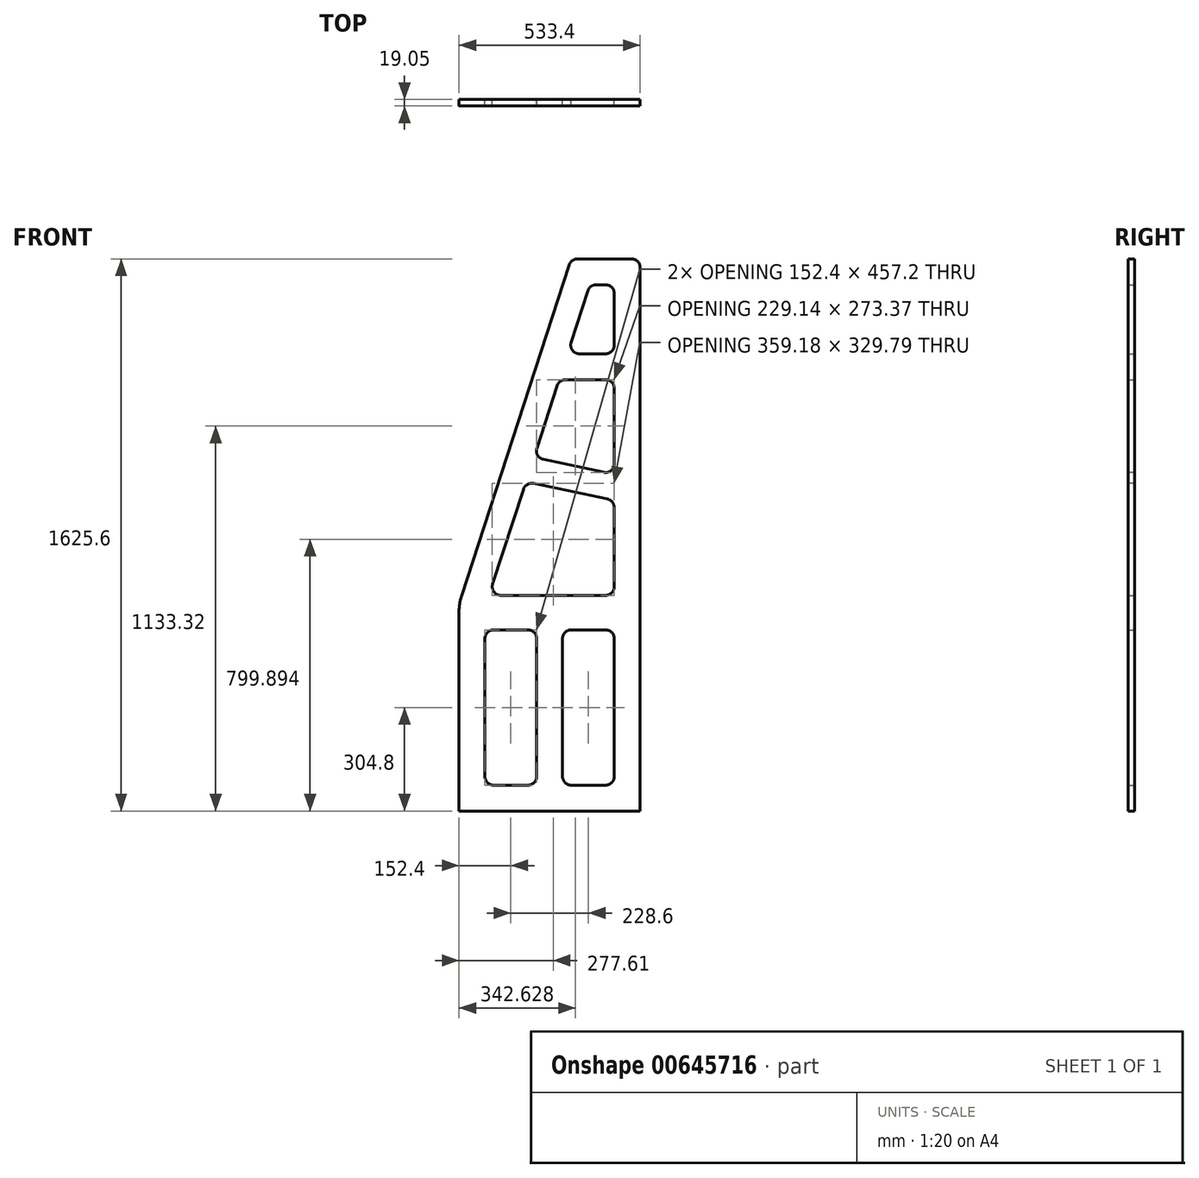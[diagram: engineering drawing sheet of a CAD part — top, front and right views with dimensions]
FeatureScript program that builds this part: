
annotation { "Feature Type Name" : "Feature", "Feature Type Description" : "" }
export const myFeature = defineFeature(function(context is Context, id is Id, definition is map)
    precondition{}
    {
        {
            var Q0;
            Q0=qCreatedBy(makeId("Front.planeOp"),FACE);
            var sketch = newSketch(context, id + "F0", { "sketchPlane" : qUnion([Q0])});
            skLineSegment(sketch, "E0.bottom", {"start": v(266.7, 812.8) * mm, "end": v(63.5, 812.8) * mm});
            skLineSegment(sketch, "E0.top", {"start": v(266.7, -812.8) * mm, "end": v(-266.7, -812.8) * mm});
            skLineSegment(sketch, "E0.left", {"start": v(266.7, 812.8) * mm, "end": v(266.7, -812.8) * mm});
            skLineSegment(sketch, "E0.right", {"start": v(-266.7, -203.2) * mm, "end": v(-266.7, -812.8) * mm});
            skPoint(sketch, "E0.middle", {"position": v(0, 0) * mm});
            skLineSegment(sketch, "E1", {"start": v(-266.7, -203.2) * mm, "end": v(63.5, 812.8) * mm});
            skPoint(sketch, "E2.orphan", {"position": v(-266.7, 812.8) * mm});
            skPoint(sketch, "E3", {"position": v(-190.5, -736.6) * mm});
            skPoint(sketch, "E4", {"position": v(190.5, -736.6) * mm});
            skPoint(sketch, "E5", {"position": v(190.5, -279.4) * mm});
            skPoint(sketch, "E6", {"position": v(38.1, -279.4) * mm});
            skPoint(sketch, "E7", {"position": v(38.1, -736.6) * mm});
            skPoint(sketch, "E8", {"position": v(-38.1, -279.4) * mm});
            skPoint(sketch, "E9", {"position": v(-38.1, -736.6) * mm});
            skPoint(sketch, "E10", {"position": v(-190.5, -279.4) * mm});
            skPoint(sketch, "E11", {"position": v(-178.32, -177.8) * mm});
            skPoint(sketch, "E12", {"position": v(190.5, -177.8) * mm});
            skPoint(sketch, "E13", {"position": v(190.5, 127) * mm});
            skPoint(sketch, "E14", {"position": v(-79.26, 127) * mm});
            skPoint(sketch, "E15", {"position": v(190.5, 228.6) * mm});
            skPoint(sketch, "E16", {"position": v(190.5, 736.6) * mm});
            skPoint(sketch, "E17", {"position": v(190.5, 457.2) * mm});
            skLineSegment(sketch, "E18", {"start": v(-190.5, -279.4) * mm, "end": v(-38.1, -279.4) * mm});
            skLineSegment(sketch, "E19", {"start": v(-38.1, -736.6) * mm, "end": v(-190.5, -736.6) * mm});
            skLineSegment(sketch, "E20", {"start": v(-190.5, -279.4) * mm, "end": v(-190.5, -736.6) * mm});
            skLineSegment(sketch, "E21", {"start": v(-38.1, -736.6) * mm, "end": v(-38.1, -279.4) * mm});
            skLineSegment(sketch, "E22", {"start": v(38.1, -279.4) * mm, "end": v(38.1, -736.6) * mm});
            skLineSegment(sketch, "E23", {"start": v(38.1, -736.6) * mm, "end": v(190.5, -736.6) * mm});
            skLineSegment(sketch, "E24", {"start": v(190.5, -736.6) * mm, "end": v(190.5, -279.4) * mm});
            skLineSegment(sketch, "E25", {"start": v(38.1, -279.4) * mm, "end": v(190.5, -279.4) * mm});
            skLineSegment(sketch, "E26", {"start": v(-178.32, -177.8) * mm, "end": v(-79.26, 127) * mm});
            skLineSegment(sketch, "E27", {"start": v(-178.32, -177.8) * mm, "end": v(190.5, -177.8) * mm});
            skLineSegment(sketch, "E28", {"start": v(190.5, -177.8) * mm, "end": v(190.5, 127) * mm});
            skPoint(sketch, "E29", {"position": v(-46.24, 228.6) * mm});
            skLineSegment(sketch, "E30", {"start": v(190.5, 228.6) * mm, "end": v(190.5, 457.2) * mm});
            skPoint(sketch, "E31", {"position": v(28.05, 457.2) * mm});
            skPoint(sketch, "E32", {"position": v(190.5, 533.4) * mm});
            skPoint(sketch, "E33", {"position": v(52.82, 533.4) * mm});
            skLineSegment(sketch, "E34", {"start": v(28.05, 457.2) * mm, "end": v(190.5, 457.2) * mm});
            skLineSegment(sketch, "E35", {"start": v(28.05, 457.2) * mm, "end": v(-46.24, 228.6) * mm});
            skLineSegment(sketch, "E36", {"start": v(190.5, 736.6) * mm, "end": v(190.5, 533.4) * mm});
            skLineSegment(sketch, "E37", {"start": v(190.5, 533.4) * mm, "end": v(52.82, 533.4) * mm});
            skLineSegment(sketch, "E38", {"start": v(190.5, 736.6) * mm, "end": v(118.68, 736.6) * mm});
            skLineSegment(sketch, "E39", {"start": v(52.82, 533.4) * mm, "end": v(118.68, 736.6) * mm});
            skPoint(sketch, "E40", {"position": v(190.5, 101.6) * mm});
            skPoint(sketch, "E41", {"position": v(190.5, 177.8) * mm});
            skLineSegment(sketch, "E42", {"start": v(-46.24, 228.6) * mm, "end": v(190.5, 177.8) * mm});
            skLineSegment(sketch, "E43", {"start": v(190.5, 177.8) * mm, "end": v(190.5, 228.6) * mm});
            skPoint(sketch, "E44", {"position": v(-69.8, 156.13) * mm});
            skLineSegment(sketch, "E45", {"start": v(-69.8, 156.13) * mm, "end": v(190.5, 101.6) * mm});
            skLineSegment(sketch, "E46", {"start": v(-79.26, 127) * mm, "end": v(-69.8, 156.13) * mm});
            skSolve(sketch);
        }
        {
            var Q0;
            Q0=makeQuery(id+"F0.imprint","IMPRINT",FACE,{"disambiguationData":[TD([[makeQuery(id+"F0.imprint","IMPRINT",EDGE,{"derivedFrom":sQuery(id+"F0.wireOp",EDGE,"E0.bottom")}),1.0]])]});
            extrude(context, id + "F1", {"entities" : qUnion([Q0]), "depth" : 19.05 * mm, "offsetDistance" : 25.4 * mm});
        }
        {
            var Q0;
            Q0=makeQuery(id+"F1.opExtrude","SWEPT_EDGE",EDGE,{"disambiguationData":[OSD([sQuery(id+"F0.wireOp",EDGE,"E34"),sQuery(id+"F0.wireOp",EDGE,"E35")])]});
            var Q1;
            Q1=makeQuery(id+"F1.opExtrude","SWEPT_EDGE",EDGE,{"disambiguationData":[OSD([sQuery(id+"F0.wireOp",EDGE,"E26"),sQuery(id+"F0.wireOp",EDGE,"GGdQVLDd-dLc8-iVr0-vvL2-QloLVLs5YIJa")])]});
            var Q2;
            Q2=makeQuery(id+"F1.opExtrude","SWEPT_EDGE",EDGE,{"disambiguationData":[OSD([sQuery(id+"F0.wireOp",EDGE,"E18"),sQuery(id+"F0.wireOp",EDGE,"E20")])]});
            var Q3;
            Q3=makeQuery(id+"F1.opExtrude","SWEPT_EDGE",EDGE,{"disambiguationData":[OSD([sQuery(id+"F0.wireOp",EDGE,"E22"),sQuery(id+"F0.wireOp",EDGE,"E25")])]});
            var Q4;
            Q4=makeQuery(id+"F1.opExtrude","SWEPT_EDGE",EDGE,{"disambiguationData":[OSD([sQuery(id+"F0.wireOp",EDGE,"E18"),sQuery(id+"F0.wireOp",EDGE,"E21")])]});
            var Q5;
            Q5=makeQuery(id+"F1.opExtrude","SWEPT_EDGE",EDGE,{"disambiguationData":[OSD([sQuery(id+"F0.wireOp",EDGE,"E24"),sQuery(id+"F0.wireOp",EDGE,"E25")])]});
            var Q6;
            Q6=makeQuery(id+"F1.opExtrude","SWEPT_EDGE",EDGE,{"disambiguationData":[OSD([sQuery(id+"F0.wireOp",EDGE,"GGdQVLDd-dLc8-iVr0-vvL2-QloLVLs5YIJa"),sQuery(id+"F0.wireOp",EDGE,"E28")])]});
            var Q7;
            Q7=makeQuery(id+"F1.opExtrude","SWEPT_EDGE",EDGE,{"disambiguationData":[OSD([sQuery(id+"F0.wireOp",EDGE,"E30"),sQuery(id+"F0.wireOp",EDGE,"E34")])]});
            var Q8;
            Q8=makeQuery(id+"F1.opExtrude","SWEPT_EDGE",EDGE,{"disambiguationData":[OSD([sQuery(id+"F0.wireOp",EDGE,"E27"),sQuery(id+"F0.wireOp",EDGE,"E28")])]});
            var Q9;
            Q9=makeQuery(id+"F1.opExtrude","SWEPT_EDGE",EDGE,{"disambiguationData":[OSD([sQuery(id+"F0.wireOp",EDGE,"E19"),sQuery(id+"F0.wireOp",EDGE,"E20")])]});
            var Q10;
            Q10=makeQuery(id+"F1.opExtrude","SWEPT_EDGE",EDGE,{"disambiguationData":[OSD([sQuery(id+"F0.wireOp",EDGE,"E22"),sQuery(id+"F0.wireOp",EDGE,"E23")])]});
            var Q11;
            Q11=makeQuery(id+"F1.opExtrude","SWEPT_EDGE",EDGE,{"disambiguationData":[OSD([sQuery(id+"F0.wireOp",EDGE,"E19"),sQuery(id+"F0.wireOp",EDGE,"E21")])]});
            var Q12;
            Q12=makeQuery(id+"F1.opExtrude","SWEPT_EDGE",EDGE,{"disambiguationData":[OSD([sQuery(id+"F0.wireOp",EDGE,"E23"),sQuery(id+"F0.wireOp",EDGE,"E24")])]});
            var Q13;
            Q13=makeQuery(id+"F1.opExtrude","SWEPT_EDGE",EDGE,{"disambiguationData":[OSD([sQuery(id+"F0.wireOp",EDGE,"E26"),sQuery(id+"F0.wireOp",EDGE,"E27")])]});
            var Q14;
            Q14=makeQuery(id+"F1.opExtrude","SWEPT_EDGE",EDGE,{"disambiguationData":[OSD([sQuery(id+"F0.wireOp",EDGE,"E67oj2bO-mtO5-RMIz-Xmbo-B9xomXMAUayS"),sQuery(id+"F0.wireOp",EDGE,"E30")])]});
            var Q15;
            Q15=makeQuery(id+"F1.opExtrude","SWEPT_EDGE",EDGE,{"disambiguationData":[OSD([sQuery(id+"F0.wireOp",EDGE,"E67oj2bO-mtO5-RMIz-Xmbo-B9xomXMAUayS"),sQuery(id+"F0.wireOp",EDGE,"E35")])]});
            var Q16;
            Q16=makeQuery(id+"F1.opExtrude","SWEPT_EDGE",EDGE,{"disambiguationData":[OSD([sQuery(id+"F0.wireOp",EDGE,"GkY00ho5-FiLZ-XiAP-ntMC-amQ00H48IU7V"),sQuery(id+"F0.wireOp",EDGE,"E36")])]});
            var Q17;
            Q17=makeQuery(id+"F1.opExtrude","SWEPT_EDGE",EDGE,{"disambiguationData":[OSD([sQuery(id+"F0.wireOp",EDGE,"E36"),sQuery(id+"F0.wireOp",EDGE,"E37")])]});
            var Q18;
            Q18=makeQuery(id+"F1.opExtrude","SWEPT_EDGE",EDGE,{"disambiguationData":[OSD([sQuery(id+"F0.wireOp",EDGE,"eTPufCVI-TwlT-T8aF-QYcv-0YaQZG3wYMVu"),sQuery(id+"F0.wireOp",EDGE,"E37")])]});
            fillet(context, id + "F2", {"entities" : qUnion([Q0, Q1, Q2, Q3, Q4, Q5, Q6, Q7, Q8, Q9, Q10, Q11, Q12, Q13, Q14, Q15, Q16, Q17, Q18]), "radius" : 25.4 * mm, "tangentPropagation" : true, "allowEdgeOverflow" : false});
        }
        {
            var Q0;
            Q0=makeQuery(id+"F1.opExtrude","SWEPT_EDGE",EDGE,{"disambiguationData":[OSD([sQuery(id+"F0.wireOp",EDGE,"E38"),sQuery(id+"F0.wireOp",EDGE,"E39")])]});
            fillet(context, id + "F3", {"entities" : qUnion([Q0]), "radius" : 25.4 * mm, "tangentPropagation" : true, "allowEdgeOverflow" : false});
        }
        {
            var Q0;
            Q0=makeQuery(id+"F1.opExtrude","SWEPT_EDGE",EDGE,{"disambiguationData":[OSD([sQuery(id+"F0.wireOp",EDGE,"E0.right"),sQuery(id+"F0.wireOp",EDGE,"E1")])]});
            fillet(context, id + "F4", {"entities" : qUnion([Q0]), "radius" : 152.4 * mm, "tangentPropagation" : true, "allowEdgeOverflow" : false});
        }
        {
            var Q0;
            Q0=makeQuery(id+"F1.opExtrude","SWEPT_EDGE",EDGE,{"disambiguationData":[OSD([sQuery(id+"F0.wireOp",EDGE,"E0.bottom"),sQuery(id+"F0.wireOp",EDGE,"E0.left")])]});
            var Q1;
            Q1=makeQuery(id+"F1.opExtrude","SWEPT_EDGE",EDGE,{"disambiguationData":[OSD([sQuery(id+"F0.wireOp",EDGE,"E0.bottom"),sQuery(id+"F0.wireOp",EDGE,"E1")])]});
            fillet(context, id + "F5", {"entities" : qUnion([Q0, Q1]), "radius" : 25.4 * mm, "tangentPropagation" : true, "allowEdgeOverflow" : false});
        }
        {
            var Q0;
            Q0=makeQuery(id+"F1.opExtrude","SWEPT_EDGE",EDGE,{"disambiguationData":[OSD([sQuery(id+"F0.wireOp",EDGE,"E45"),sQuery(id+"F0.wireOp",EDGE,"E46")])]});
            var Q1;
            Q1=makeQuery(id+"F1.opExtrude","SWEPT_EDGE",EDGE,{"disambiguationData":[OSD([sQuery(id+"F0.wireOp",EDGE,"E42"),sQuery(id+"F0.wireOp",EDGE,"E43")])]});
            fillet(context, id + "F6", {"entities" : qUnion([Q0, Q1]), "radius" : 25.4 * mm, "tangentPropagation" : true, "allowEdgeOverflow" : false});
        }
    });
